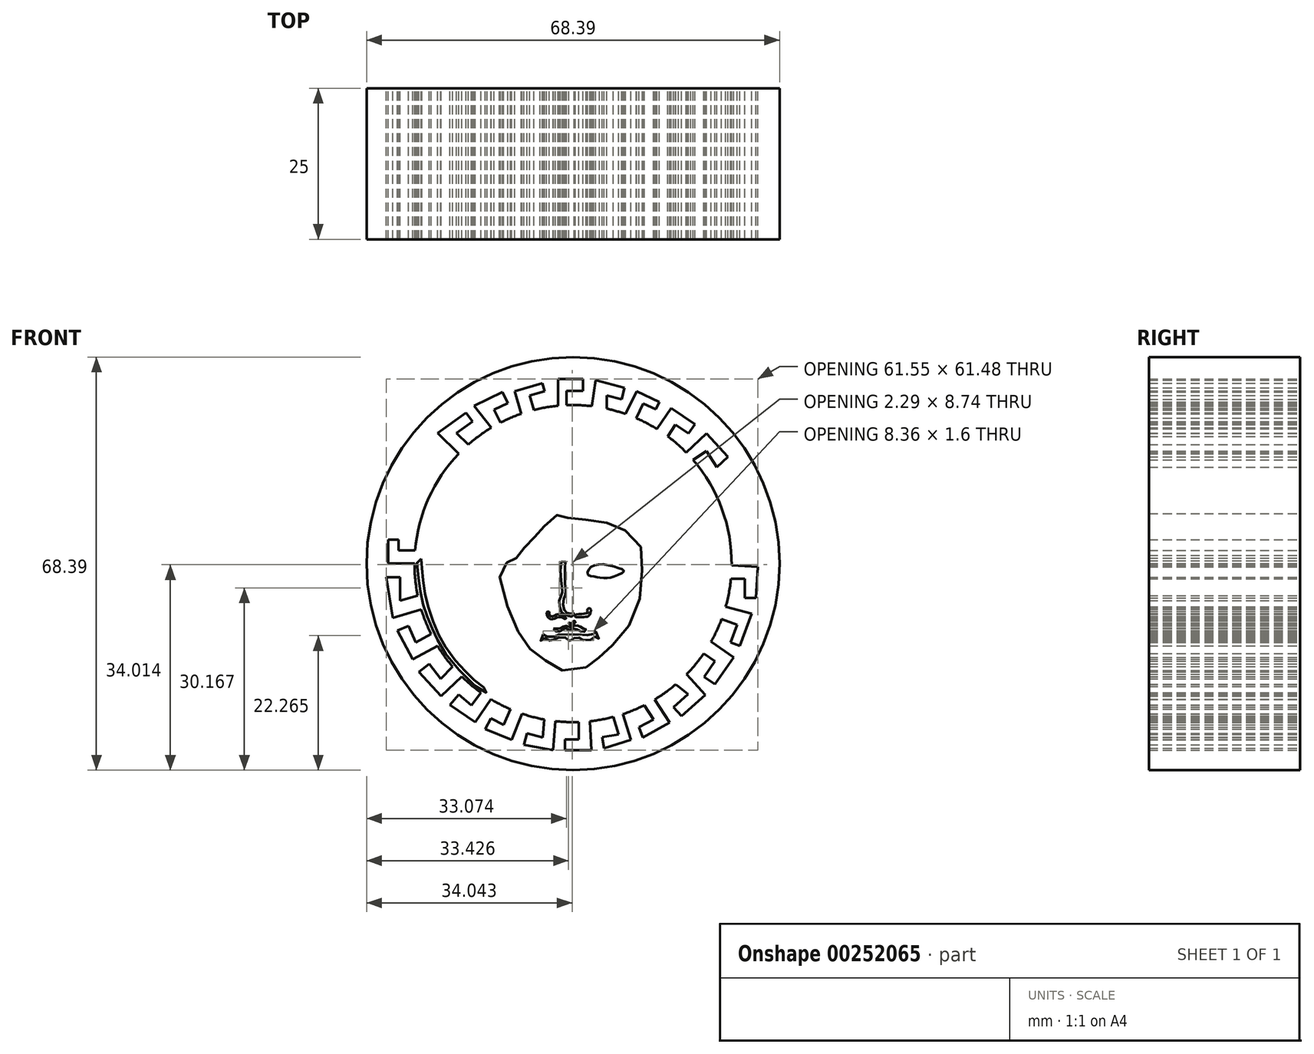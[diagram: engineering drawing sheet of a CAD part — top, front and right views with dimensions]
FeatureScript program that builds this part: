
annotation { "Feature Type Name" : "Feature", "Feature Type Description" : "" }
export const myFeature = defineFeature(function(context is Context, id is Id, definition is map)
    precondition{}
    {
        {
            var Q0;
            Q0=qCreatedBy(makeId("Front.planeOp"),FACE);
            var sketch = newSketch(context, id + "F0", { "sketchPlane" : qUnion([Q0])});
            skCircle(sketch, "E0", {"center": v(-32.8, 36.71) * mm, "radius": 32.75 * mm});
            skCircle(sketch, "E1", {"center": v(-32.8, 36.71) * mm, "radius": 34.2 * mm});
            skCircle(sketch, "E2", {"center": v(-32.8, 36.71) * mm, "radius": 26.26 * mm});
            skLineSegment(sketch, "E3", {"start": v(-41.39, 61.53) * mm, "end": v(-42.48, 65.23) * mm});
            skLineSegment(sketch, "E4", {"start": v(-42.48, 65.23) * mm, "end": v(-37.91, 66.57) * mm});
            skLineSegment(sketch, "E5", {"start": v(-37.91, 66.57) * mm, "end": v(-37.53, 65.26) * mm});
            skLineSegment(sketch, "E6", {"start": v(-37.53, 65.26) * mm, "end": v(-39.96, 64.55) * mm});
            skLineSegment(sketch, "E7", {"start": v(-39.96, 64.55) * mm, "end": v(-39.26, 62.16) * mm});
            skLineSegment(sketch, "E8", {"start": v(-35.28, 62.85) * mm, "end": v(-35.28, 67.28) * mm});
            skLineSegment(sketch, "E9", {"start": v(-35.28, 67.28) * mm, "end": v(-31.19, 67.28) * mm});
            skLineSegment(sketch, "E10", {"start": v(-31.19, 67.28) * mm, "end": v(-31.19, 65.3) * mm});
            skLineSegment(sketch, "E11", {"start": v(-31.19, 65.3) * mm, "end": v(-33.87, 65.3) * mm});
            skLineSegment(sketch, "E12", {"start": v(-33.87, 65.3) * mm, "end": v(-33.87, 62.95) * mm});
            skLineSegment(sketch, "E13", {"start": v(-29.7, 62.79) * mm, "end": v(-29.07, 67.06) * mm});
            skLineSegment(sketch, "E14", {"start": v(-29.07, 67.06) * mm, "end": v(-24.27, 65.8) * mm});
            skLineSegment(sketch, "E15", {"start": v(-24.27, 65.8) * mm, "end": v(-24.76, 63.92) * mm});
            skLineSegment(sketch, "E16", {"start": v(-24.76, 63.92) * mm, "end": v(-27.2, 64.57) * mm});
            skLineSegment(sketch, "E17", {"start": v(-27.2, 64.57) * mm, "end": v(-27.2, 62.37) * mm});
            skLineSegment(sketch, "E18", {"start": v(-24.08, 61.48) * mm, "end": v(-22.3, 65.26) * mm});
            skLineSegment(sketch, "E19", {"start": v(-22.3, 65.26) * mm, "end": v(-18.54, 63.49) * mm});
            skLineSegment(sketch, "E20", {"start": v(-18.54, 63.49) * mm, "end": v(-19.12, 62.27) * mm});
            skLineSegment(sketch, "E21", {"start": v(-19.12, 62.27) * mm, "end": v(-21.2, 63.25) * mm});
            skLineSegment(sketch, "E22", {"start": v(-21.2, 63.25) * mm, "end": v(-22.35, 60.8) * mm});
            skLineSegment(sketch, "E23", {"start": v(-18.92, 59) * mm, "end": v(-16.58, 62.48) * mm});
            skLineSegment(sketch, "E24", {"start": v(-16.58, 62.48) * mm, "end": v(-12.61, 59.8) * mm});
            skLineSegment(sketch, "E25", {"start": v(-12.61, 59.8) * mm, "end": v(-13.66, 58.25) * mm});
            skLineSegment(sketch, "E26", {"start": v(-13.66, 58.25) * mm, "end": v(-15.83, 59.71) * mm});
            skLineSegment(sketch, "E27", {"start": v(-15.83, 59.71) * mm, "end": v(-17.13, 57.79) * mm});
            skLineSegment(sketch, "E28", {"start": v(-14.07, 55.12) * mm, "end": v(-10.72, 58.24) * mm});
            skLineSegment(sketch, "E29", {"start": v(-10.72, 58.24) * mm, "end": v(-7.13, 54.4) * mm});
            skLineSegment(sketch, "E30", {"start": v(-7.13, 54.4) * mm, "end": v(-8.98, 52.67) * mm});
            skLineSegment(sketch, "E31", {"start": v(-8.98, 52.67) * mm, "end": v(-10.72, 55.35) * mm});
            skLineSegment(sketch, "E32", {"start": v(-10.72, 55.35) * mm, "end": v(-12.95, 53.9) * mm});
            skLineSegment(sketch, "E33", {"start": v(-44.83, 60.05) * mm, "end": v(-45.87, 62.2) * mm});
            skLineSegment(sketch, "E34", {"start": v(-45.87, 62.2) * mm, "end": v(-43.6, 63.3) * mm});
            skLineSegment(sketch, "E35", {"start": v(-43.6, 63.3) * mm, "end": v(-44.5, 65.14) * mm});
            skLineSegment(sketch, "E36", {"start": v(-44.5, 65.14) * mm, "end": v(-49.2, 62.86) * mm});
            skLineSegment(sketch, "E37", {"start": v(-49.2, 62.86) * mm, "end": v(-46.33, 59.22) * mm});
            skLineSegment(sketch, "E38", {"start": v(-50.16, 56.4) * mm, "end": v(-52.08, 58.31) * mm});
            skLineSegment(sketch, "E39", {"start": v(-52.08, 58.31) * mm, "end": v(-49.47, 60.22) * mm});
            skLineSegment(sketch, "E40", {"start": v(-49.47, 60.22) * mm, "end": v(-50.55, 61.71) * mm});
            skLineSegment(sketch, "E41", {"start": v(-50.55, 61.71) * mm, "end": v(-55.2, 58.32) * mm});
            skLineSegment(sketch, "E42", {"start": v(-55.2, 58.32) * mm, "end": v(-51.76, 54.88) * mm});
            skLineSegment(sketch, "E43", {"start": v(-59.05, 36.72) * mm, "end": v(-63.44, 36.72) * mm});
            skLineSegment(sketch, "E44", {"start": v(-63.44, 36.72) * mm, "end": v(-63.44, 40.67) * mm});
            skLineSegment(sketch, "E45", {"start": v(-63.44, 40.67) * mm, "end": v(-61.67, 40.67) * mm});
            skLineSegment(sketch, "E46", {"start": v(-61.67, 40.67) * mm, "end": v(-61.67, 38.9) * mm});
            skLineSegment(sketch, "E47", {"start": v(-61.67, 38.9) * mm, "end": v(-58.96, 38.9) * mm});
            skLineSegment(sketch, "E48", {"start": v(-58.5, 31.4) * mm, "end": v(-61.46, 30.58) * mm});
            skLineSegment(sketch, "E49", {"start": v(-61.46, 30.58) * mm, "end": v(-61.46, 34.46) * mm});
            skLineSegment(sketch, "E50", {"start": v(-61.46, 34.46) * mm, "end": v(-63.72, 34.46) * mm});
            skLineSegment(sketch, "E51", {"start": v(-63.72, 34.46) * mm, "end": v(-62.66, 27.75) * mm});
            skLineSegment(sketch, "E52", {"start": v(-62.66, 27.75) * mm, "end": v(-57.94, 29.15) * mm});
            skLineSegment(sketch, "E53", {"start": v(-56.32, 25.04) * mm, "end": v(-58.82, 23.66) * mm});
            skLineSegment(sketch, "E54", {"start": v(-58.82, 23.66) * mm, "end": v(-60.02, 26.4) * mm});
            skLineSegment(sketch, "E55", {"start": v(-60.02, 26.4) * mm, "end": v(-61.86, 25.6) * mm});
            skLineSegment(sketch, "E56", {"start": v(-61.86, 25.6) * mm, "end": v(-59.32, 20.89) * mm});
            skLineSegment(sketch, "E57", {"start": v(-59.32, 20.89) * mm, "end": v(-55.24, 23.09) * mm});
            skLineSegment(sketch, "E58", {"start": v(-52.77, 19.67) * mm, "end": v(-54.68, 17.64) * mm});
            skLineSegment(sketch, "E59", {"start": v(-54.68, 17.64) * mm, "end": v(-56.6, 20.12) * mm});
            skLineSegment(sketch, "E60", {"start": v(-56.6, 20.12) * mm, "end": v(-58.36, 18.75) * mm});
            skLineSegment(sketch, "E61", {"start": v(-58.36, 18.75) * mm, "end": v(-54.66, 14.78) * mm});
            skLineSegment(sketch, "E62", {"start": v(-54.66, 14.78) * mm, "end": v(-51.2, 17.99) * mm});
            skLineSegment(sketch, "E63", {"start": v(-48.05, 15.34) * mm, "end": v(-49.62, 13.23) * mm});
            skLineSegment(sketch, "E64", {"start": v(-49.62, 13.23) * mm, "end": v(-51.71, 15.02) * mm});
            skLineSegment(sketch, "E65", {"start": v(-51.71, 15.02) * mm, "end": v(-53.2, 13.3) * mm});
            skLineSegment(sketch, "E66", {"start": v(-53.2, 13.3) * mm, "end": v(-49, 10.43) * mm});
            skLineSegment(sketch, "E67", {"start": v(-49, 10.43) * mm, "end": v(-46.4, 14.25) * mm});
            skLineSegment(sketch, "E68", {"start": v(-43.18, 12.6) * mm, "end": v(-44.28, 9.98) * mm});
            skLineSegment(sketch, "E69", {"start": v(-44.28, 9.98) * mm, "end": v(-46.42, 11.1) * mm});
            skLineSegment(sketch, "E70", {"start": v(-46.42, 11.1) * mm, "end": v(-47.38, 9.28) * mm});
            skLineSegment(sketch, "E71", {"start": v(-47.38, 9.28) * mm, "end": v(-42.95, 7.51) * mm});
            skLineSegment(sketch, "E72", {"start": v(-42.95, 7.51) * mm, "end": v(-41.23, 11.85) * mm});
            skLineSegment(sketch, "E73", {"start": v(-37.59, 10.9) * mm, "end": v(-37.84, 7.91) * mm});
            skLineSegment(sketch, "E74", {"start": v(-37.84, 7.91) * mm, "end": v(-40.43, 8.59) * mm});
            skLineSegment(sketch, "E75", {"start": v(-40.43, 8.59) * mm, "end": v(-40.92, 6.72) * mm});
            skLineSegment(sketch, "E76", {"start": v(-40.92, 6.72) * mm, "end": v(-36.12, 5.8) * mm});
            skLineSegment(sketch, "E77", {"start": v(-36.12, 5.8) * mm, "end": v(-35.73, 10.62) * mm});
            skLineSegment(sketch, "E78", {"start": v(-31.85, 10.47) * mm, "end": v(-31.85, 7.56) * mm});
            skLineSegment(sketch, "E79", {"start": v(-31.85, 7.56) * mm, "end": v(-34.15, 7.56) * mm});
            skLineSegment(sketch, "E80", {"start": v(-34.15, 7.56) * mm, "end": v(-34.15, 5.82) * mm});
            skLineSegment(sketch, "E81", {"start": v(-34.15, 5.82) * mm, "end": v(-29.73, 5.82) * mm});
            skLineSegment(sketch, "E82", {"start": v(-29.73, 5.82) * mm, "end": v(-30, 10.6) * mm});
            skLineSegment(sketch, "E83", {"start": v(-26.15, 11.31) * mm, "end": v(-25.27, 8.44) * mm});
            skLineSegment(sketch, "E84", {"start": v(-25.27, 8.44) * mm, "end": v(-28, 7.96) * mm});
            skLineSegment(sketch, "E85", {"start": v(-28, 7.96) * mm, "end": v(-27.68, 6.11) * mm});
            skLineSegment(sketch, "E86", {"start": v(-27.68, 6.11) * mm, "end": v(-23.2, 7.55) * mm});
            skLineSegment(sketch, "E87", {"start": v(-23.2, 7.55) * mm, "end": v(-24.55, 11.78) * mm});
            skLineSegment(sketch, "E88", {"start": v(-21.02, 13.25) * mm, "end": v(-19.46, 10.87) * mm});
            skLineSegment(sketch, "E89", {"start": v(-19.46, 10.87) * mm, "end": v(-21.86, 9.6) * mm});
            skLineSegment(sketch, "E90", {"start": v(-21.86, 9.6) * mm, "end": v(-21.27, 7.94) * mm});
            skLineSegment(sketch, "E91", {"start": v(-21.27, 7.94) * mm, "end": v(-16.82, 10.37) * mm});
            skLineSegment(sketch, "E92", {"start": v(-16.82, 10.37) * mm, "end": v(-19.26, 14.21) * mm});
            skLineSegment(sketch, "E93", {"start": v(-15.8, 16.7) * mm, "end": v(-15.33, 16.33) * mm});
            skLineSegment(sketch, "E94", {"start": v(-15.33, 16.33) * mm, "end": v(-13.76, 15.09) * mm});
            skLineSegment(sketch, "E95", {"start": v(-13.76, 15.09) * mm, "end": v(-16.16, 12.92) * mm});
            skLineSegment(sketch, "E96", {"start": v(-16.16, 12.92) * mm, "end": v(-14.83, 11.44) * mm});
            skLineSegment(sketch, "E97", {"start": v(-14.83, 11.44) * mm, "end": v(-10.91, 14.97) * mm});
            skLineSegment(sketch, "E98", {"start": v(-10.91, 14.97) * mm, "end": v(-13.3, 17.62) * mm});
            skLineSegment(sketch, "E99", {"start": v(-13.3, 17.62) * mm, "end": v(-14.02, 18.36) * mm});
            skLineSegment(sketch, "E100", {"start": v(-11.18, 21.81) * mm, "end": v(-9.32, 20.53) * mm});
            skLineSegment(sketch, "E101", {"start": v(-9.32, 20.53) * mm, "end": v(-11.1, 17.98) * mm});
            skLineSegment(sketch, "E102", {"start": v(-11.1, 17.98) * mm, "end": v(-9.3, 16.73) * mm});
            skLineSegment(sketch, "E103", {"start": v(-9.3, 16.73) * mm, "end": v(-6.2, 21.2) * mm});
            skLineSegment(sketch, "E104", {"start": v(-6.2, 21.2) * mm, "end": v(-9.94, 23.8) * mm});
            skLineSegment(sketch, "E105", {"start": v(-8.2, 27.51) * mm, "end": v(-5.64, 26.58) * mm});
            skLineSegment(sketch, "E106", {"start": v(-5.64, 26.58) * mm, "end": v(-6.72, 23.63) * mm});
            skLineSegment(sketch, "E107", {"start": v(-6.72, 23.63) * mm, "end": v(-5.19, 23.08) * mm});
            skLineSegment(sketch, "E108", {"start": v(-5.19, 23.08) * mm, "end": v(-3.24, 28.44) * mm});
            skLineSegment(sketch, "E109", {"start": v(-3.24, 28.44) * mm, "end": v(-7.52, 29.6) * mm});
            skLineSegment(sketch, "E110", {"start": v(-6.66, 34.18) * mm, "end": v(-4.34, 34.18) * mm});
            skLineSegment(sketch, "E111", {"start": v(-4.34, 34.18) * mm, "end": v(-4.34, 31.03) * mm});
            skLineSegment(sketch, "E112", {"start": v(-4.34, 31.03) * mm, "end": v(-2.5, 31.03) * mm});
            skLineSegment(sketch, "E113", {"start": v(-2.5, 31.03) * mm, "end": v(-2.17, 36.17) * mm});
            skLineSegment(sketch, "E114", {"start": v(-2.17, 36.17) * mm, "end": v(-6.54, 36.44) * mm});
            skFitSpline(sketch, "E115", {"points": [v(-57.98, 37.5) * mm, v(-58.5, 37.55) * mm, v(-58.48, 35.14) * mm, v(-58.11, 32.23) * mm, v(-57.58, 29.69) * mm, v(-56.69, 27.31) * mm, v(-55.74, 25.13) * mm, v(-54.4, 22.5) * mm, v(-50.12, 17.48) * mm, v(-47.19, 15.36) * mm, v(-47.1, 15.8) * mm, v(-48.05, 16.47) * mm, v(-49.84, 18.1) * mm, v(-51.6, 19.88) * mm, v(-54.09, 23.12) * mm, v(-55.26, 25.39) * mm, v(-56.63, 28.93) * mm, v(-57.27, 31.5) * mm, v(-57.7, 34.24) * mm, v(-57.83, 36.3) * mm, v(-57.98, 37.5) * mm]});
            skFitSpline(sketch, "E116", {"points": [v(-21.57, 39.47) * mm, v(-21.34, 36.3) * mm, v(-21.65, 31.48) * mm, v(-23.31, 26.82) * mm, v(-25.92, 23.5) * mm, v(-27.66, 22.08) * mm, v(-29, 20.58) * mm, v(-30.03, 19.7) * mm, v(-33.27, 19.24) * mm, v(-35.8, 19.16) * mm, v(-37.93, 21.21) * mm, v(-39.67, 22.4) * mm, v(-41.1, 23.98) * mm, v(-42.83, 27.53) * mm, v(-44.5, 32.2) * mm, v(-44.8, 36.23) * mm, v(-43.7, 36.94) * mm, v(-42.83, 38.04) * mm, v(-42.2, 37.65) * mm, v(-41.1, 38.28) * mm, v(-40.86, 39.47) * mm, v(-40.3, 40.33) * mm, v(-38.64, 41.52) * mm, v(-37.54, 42.63) * mm, v(-37.54, 43.02) * mm, v(-36.04, 44.2) * mm, v(-35, 45) * mm, v(-34.3, 44.44) * mm, v(-33.27, 44.29) * mm, v(-31.14, 44.05) * mm, v(-28.37, 43.65) * mm, v(-25.92, 43.1) * mm, v(-23.7, 41.84) * mm, v(-21.57, 39.47) * mm]});
            skFitSpline(sketch, "E117", {"points": [v(-34.69, 37.06) * mm, v(-34.78, 34) * mm, v(-34.64, 32.83) * mm, v(-34.63, 31.77) * mm, v(-34.91, 31.15) * mm, v(-35.09, 30.66) * mm, v(-35.04, 29.51) * mm, v(-34.6, 28.54) * mm, v(-33.6, 28.04) * mm, v(-32.76, 28.03) * mm, v(-32.59, 28.45) * mm, v(-33.02, 28.44) * mm, v(-33.58, 28.49) * mm, v(-34.05, 28.73) * mm, v(-34.34, 29.32) * mm, v(-34.43, 30.4) * mm, v(-34.17, 31.25) * mm, v(-34.04, 31.62) * mm, v(-34.07, 32.65) * mm, v(-34.16, 34.48) * mm, v(-34.1, 36.55) * mm, v(-34.1, 37.08) * mm, v(-34.69, 37.06) * mm]});
            skFitSpline(sketch, "E118", {"points": [v(-37.16, 28.55) * mm, v(-37.07, 28.06) * mm, v(-36.63, 27.52) * mm, v(-36.21, 27.52) * mm, v(-35.96, 27.52) * mm, v(-35.56, 27.78) * mm, v(-35.1, 27.87) * mm, v(-34.73, 27.84) * mm, v(-34.44, 27.7) * mm, v(-34.27, 27.56) * mm, v(-33.94, 27.64) * mm, v(-34.1, 27.88) * mm, v(-34.3, 27.98) * mm, v(-34.6, 28.22) * mm, v(-34.91, 28.31) * mm, v(-35.49, 28.27) * mm, v(-35.78, 28.13) * mm, v(-36.3, 28) * mm, v(-36.69, 28.08) * mm, v(-36.73, 28.6) * mm, v(-36.83, 28.76) * mm, v(-37.1, 28.75) * mm, v(-37.16, 28.55) * mm]});
            skFitSpline(sketch, "E119", {"points": [v(-32.27, 28.27) * mm, v(-32.51, 27.95) * mm, v(-32.1, 27.87) * mm, v(-31.77, 27.85) * mm, v(-31.24, 27.85) * mm, v(-30.75, 27.9) * mm, v(-30.36, 27.92) * mm, v(-30.16, 28.15) * mm, v(-29.93, 28.5) * mm, v(-29.84, 29.15) * mm, v(-30, 29.26) * mm, v(-30.22, 29.3) * mm, v(-30.44, 29.03) * mm, v(-30.39, 28.79) * mm, v(-30.39, 28.62) * mm, v(-30.47, 28.5) * mm, v(-30.72, 28.45) * mm, v(-31.34, 28.38) * mm, v(-32.27, 28.27) * mm]});
            skFitSpline(sketch, "E120", {"points": [v(-33.48, 26.9) * mm, v(-33.37, 26.65) * mm, v(-32.66, 26.62) * mm, v(-32.63, 26.83) * mm, v(-32.53, 26.93) * mm, v(-32.4, 26.94) * mm, v(-32.53, 27.2) * mm, v(-32.76, 27.18) * mm, v(-32.81, 26.97) * mm, v(-32.93, 26.82) * mm, v(-33.16, 26.83) * mm, v(-33.48, 26.9) * mm]});
            skFitSpline(sketch, "E121", {"points": [v(-36.04, 25.94) * mm, v(-35.87, 25.57) * mm, v(-35.19, 25.46) * mm, v(-34.81, 25.56) * mm, v(-34.52, 25.8) * mm, v(-34.32, 25.9) * mm, v(-34.2, 25.95) * mm, v(-33.82, 26.02) * mm, v(-33.57, 25.8) * mm, v(-33.29, 25.67) * mm, v(-33.08, 25.66) * mm, v(-33.02, 25.66) * mm, v(-32.87, 25.9) * mm, v(-32.53, 25.92) * mm, v(-31.9, 25.75) * mm, v(-31.5, 25.48) * mm, v(-31.15, 25.4) * mm, v(-30.72, 25.52) * mm, v(-30.65, 25.78) * mm, v(-30.83, 26.05) * mm, v(-31.2, 25.95) * mm, v(-31.53, 26.19) * mm, v(-31.78, 26.36) * mm, v(-32.19, 26.44) * mm, v(-32.48, 26.45) * mm, v(-32.86, 26.3) * mm, v(-33, 26.16) * mm, v(-33.16, 26.03) * mm, v(-33.39, 26.24) * mm, v(-33.67, 26.37) * mm, v(-33.96, 26.4) * mm, v(-34.28, 26.4) * mm, v(-34.6, 26.16) * mm, v(-34.85, 26) * mm, v(-35.08, 25.96) * mm, v(-35.27, 25.92) * mm, v(-35.5, 25.92) * mm, v(-35.57, 25.92) * mm, v(-35.76, 26) * mm, v(-35.93, 26.06) * mm, v(-36.04, 25.94) * mm]});
            skFitSpline(sketch, "E122", {"points": [v(-37.75, 25) * mm, v(-38.23, 24.39) * mm, v(-38.1, 23.85) * mm, v(-37.66, 24) * mm, v(-37.52, 24.33) * mm, v(-37.27, 24.13) * mm, v(-36.87, 24) * mm, v(-36.64, 23.97) * mm, v(-36.52, 23.97) * mm, v(-36.2, 23.98) * mm, v(-35.98, 24.13) * mm, v(-35.5, 24.34) * mm, v(-35, 24.54) * mm, v(-34.4, 24.62) * mm, v(-34.04, 24.41) * mm, v(-33.82, 24.16) * mm, v(-33.46, 23.97) * mm, v(-33.1, 23.95) * mm, v(-32.84, 24.05) * mm, v(-32.66, 24.34) * mm, v(-32.3, 24.55) * mm, v(-31.88, 24.48) * mm, v(-31.65, 24.34) * mm, v(-31.43, 24.15) * mm, v(-31.03, 24.04) * mm, v(-30.5, 24.04) * mm, v(-29.73, 24.13) * mm, v(-29.56, 24.27) * mm, v(-29.42, 24.4) * mm, v(-29.06, 24.64) * mm, v(-28.8, 24.34) * mm, v(-28.55, 24.3) * mm, v(-28.46, 24.65) * mm, v(-29.17, 25.59) * mm, v(-29.42, 25.56) * mm, v(-29.55, 25.24) * mm, v(-29.4, 24.93) * mm, v(-30.16, 24.89) * mm, v(-30.9, 24.85) * mm, v(-31.25, 24.85) * mm, v(-31.72, 25.06) * mm, v(-32.53, 25.08) * mm, v(-33.18, 24.57) * mm, v(-33.76, 25.03) * mm, v(-34.9, 25.03) * mm, v(-35.22, 24.89) * mm, v(-35.52, 24.73) * mm, v(-36.08, 24.58) * mm, v(-36.63, 24.51) * mm, v(-37.17, 24.7) * mm, v(-37.28, 25.03) * mm, v(-37.75, 25) * mm]});
            skFitSpline(sketch, "E123", {"points": [v(-30.2, 35.75) * mm, v(-29.03, 36.5) * mm, v(-27.1, 36.5) * mm, v(-25.6, 36.08) * mm, v(-24.38, 35.52) * mm, v(-25.65, 34.72) * mm, v(-27.01, 34.34) * mm, v(-28.42, 34.39) * mm, v(-29.36, 34.58) * mm, v(-30.35, 34.9) * mm, v(-30.2, 35.75) * mm]});
            skSolve(sketch);
        }
        {
            var Q0;
            Q0=makeQuery(id+"F0.imprint","IMPRINT",FACE,{"disambiguationData":[TD([[makeQuery(id+"F0.imprint","IMPRINT",EDGE,{"derivedFrom":sQuery(id+"F0.wireOp",EDGE,"E0")}),-1.0]])]});
            var Q1;
            Q1=makeQuery(id+"F0.imprint","IMPRINT",FACE,{"disambiguationData":[TD([[makeQuery(id+"F0.imprint","IMPRINT",EDGE,{"derivedFrom":sQuery(id+"F0.wireOp",EDGE,"E0")}),1.0]])]});
            var Q2;
            Q2=makeQuery(id+"F0.imprint","IMPRINT",FACE,{"disambiguationData":[TD([[makeQuery(id+"F0.imprint","IMPRINT",EDGE,{"derivedFrom":sQuery(id+"F0.wireOp",EDGE,"E115")}),1.0]])]});
            var Q3;
            Q3=makeQuery(id+"F0.imprint","IMPRINT",FACE,{"disambiguationData":[TD([[makeQuery(id+"F0.imprint","IMPRINT",EDGE,{"derivedFrom":sQuery(id+"F0.wireOp",EDGE,"E116")}),-1.0]])]});
            extrude(context, id + "F1", {"entities" : qUnion([Q0, Q1, Q2, Q3]), "depth" : 25 * mm, "offsetDistance" : 25 * mm});
        }
    });
